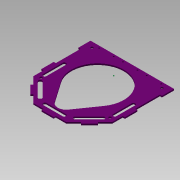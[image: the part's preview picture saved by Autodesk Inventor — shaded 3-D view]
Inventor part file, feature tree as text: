
AUTODESK INVENTOR PART (.ipt)
format: ipt  version: 2015 SP1 (Build 190203100, 203)  size: 274,432 bytes
history: native  units: mm
features: sketch x7, extrude x5, plane x1
ambient origin geometry x8: Origin, YZ Plane, XZ Plane, XY Plane, X Axis, Y Axis, Z Axis, Center Point
bodies: Body1 (feature_tree)
feature tree (13):
  sketch  "Sketch1"  dims[d10=3.0mm d11=3.0mm]
  plane  "Work Plane2"
  sketch  "Sketch2"  dims[d12=135.0deg d14=3.0mm]
  extrude  "Extrusion4"  Depth=3.0mm
  extrude  "Extrusion5"  Depth=3.0mm
  extrude  "Extrusion6"  Depth=3.0mm
  sketch  "Sketch4"  dims[d17=3.0mm d18=3.0mm]
  extrude  "Extrusion7"  Depth=3.0mm
  sketch  "Sketch6"  dims[d24=2.0mm]
  extrude  "Extrusion9"  Depth=3.0mm TaperAngle=0.0deg
  sketch  "Sketch3"  dims[d15=3.0mm d16=3.0mm]
  sketch  "Sketch5"  dims[d19=2.0mm d20=0.0mm d21=3.0mm d22=0.0mm]
  sketch  "Sketch8"  dims[d25=2.0mm d26=2.0mm d27=2.0mm d28=6.0mm d29=6.0mm d30=21.0mm d31=21.0mm d32=3.0mm d33=12.5mm d35=12.5mm d36=2.0mm d37=2.0mm d38=2.0mm d39=21.0mm d40=21.0mm d41=10.5mm d42=10.5mm d43=10.0mm d44=0.0mm d45=10.0mm d46=0.0mm d54=5.0mm d68=2.0mm d71=2.0mm d72=10.0mm d73=0.0mm d74=6.0mm d76=6.0mm d77=6.0mm d78=6.0mm d79=6.0mm]
